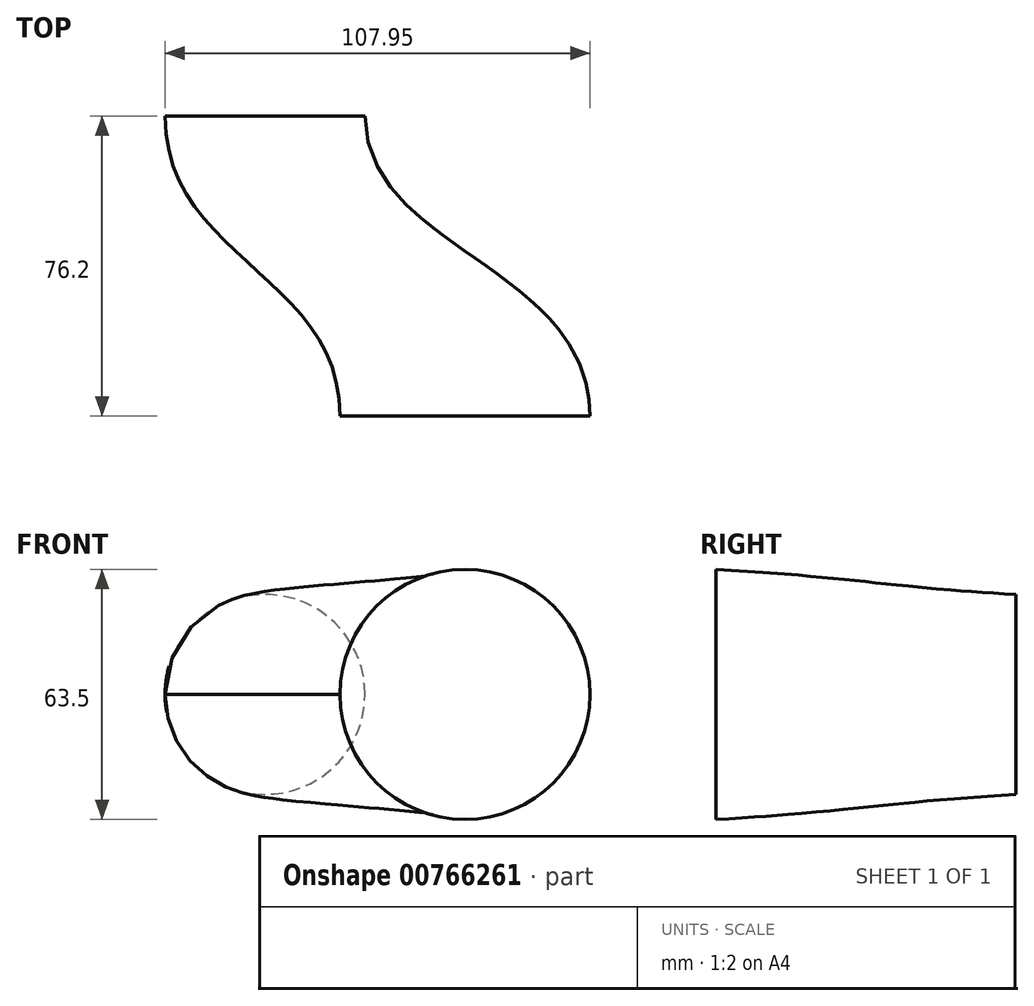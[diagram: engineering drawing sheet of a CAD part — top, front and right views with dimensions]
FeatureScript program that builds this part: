
annotation { "Feature Type Name" : "Feature", "Feature Type Description" : "" }
export const myFeature = defineFeature(function(context is Context, id is Id, definition is map)
    precondition{}
    {
        {
            var Q0;
            Q0=qCreatedBy(makeId("Front.planeOp"),FACE);
            cPlane(context, id + "F0", {"entities" : qUnion([Q0]), "cplaneType" : CPlaneType.OFFSET, "offset" : 76.2 * mm, "width" : 152.4 * mm, "height" : 152.4 * mm});
        }
        {
            var Q0;
            Q0=qCreatedBy(id+"F0.planeOp",FACE);
            var sketch = newSketch(context, id + "F1", { "sketchPlane" : qUnion([Q0])});
            skCircle(sketch, "E0", {"center": v(0, 0) * mm, "radius": 31.75 * mm});
            skSolve(sketch);
        }
        {
            var Q0;
            Q0=qCreatedBy(makeId("Front.planeOp"),FACE);
            var sketch = newSketch(context, id + "F2", { "sketchPlane" : qUnion([Q0])});
            skCircle(sketch, "E1", {"center": v(-50.8, 0) * mm, "radius": 25.4 * mm});
            skLineSegment(sketch, "E2", {"start": v(-50.8, 0) * mm, "end": v(0, 0) * mm, "construction": true});
            skSolve(sketch);
        }
        {
            var Q0;
            Q0=qCreatedBy(makeId("Top.planeOp"),FACE);
            var sketch = newSketch(context, id + "F3", { "sketchPlane" : qUnion([Q0])});
            skFitSpline(sketch, "E3", {"points": [v(-76.2, 0) * mm, v(-31.75, -76.2) * mm], "startDerivative": vector(0, -108.7) * mm, "endDerivative": vector(0, -107.18) * mm});
            skSolve(sketch);
        }
        {
            var Q0;
            Q0=qCreatedBy(makeId("Top.planeOp"),FACE);
            var sketch = newSketch(context, id + "F4", { "sketchPlane" : qUnion([Q0])});
            skFitSpline(sketch, "E4", {"points": [v(-25.4, 0) * mm, v(31.75, -76.2) * mm], "startDerivative": vector(0, -101.66) * mm, "endDerivative": vector(0, -114.17) * mm});
            skSolve(sketch);
        }
        {
            var Q0;
            Q0=makeQuery(id+"F2.imprint","IMPRINT",FACE,{"disambiguationData":[TD([[makeQuery(id+"F2.imprint","IMPRINT",EDGE,{"derivedFrom":sQuery(id+"F2.wireOp",EDGE,"E1")}),1.0]])]});
            var Q1;
            Q1=makeQuery(id+"F1.imprint","IMPRINT",FACE,{"disambiguationData":[TD([[makeQuery(id+"F1.imprint","IMPRINT",EDGE,{"derivedFrom":sQuery(id+"F1.wireOp",EDGE,"E0")}),1.0]])]});
            var Q2;
            Q2 = qConstructionFilter(qBodyType(qCreatedBy(id + "F3" ,EDGE), BodyType.WIRE), ConstructionObject.NO);
            var Q3;
            Q3 = qConstructionFilter(qBodyType(qCreatedBy(id + "F4" ,EDGE), BodyType.WIRE), ConstructionObject.NO);
            var Q4;
            Q4=sQuery(id+"F3.wireOp",VERTEX,"qpPcSAEk-Yxff-x6JP-xup5-S4P08pdUFl33.start");
            var Q5;
            Q5=sQuery(id+"F3.wireOp",VERTEX,"snNEfOa5-MTmY-YXjU-iu0s-ZxJhTdPCbkap.start");
            loft(context, id + "F5", {"addGuides" : true, "sheetProfilesArray" : [{ "sheetProfileEntities" : qUnion([Q0]) }, { "sheetProfileEntities" : qUnion([Q1]) }], "guidesArray" : [{ "guideEntities" : qUnion([Q2]), "guideDerivativeType" : LoftGuideDerivativeType.DEFAULT, "guideDerivativeMagnitude" : 1 }, { "guideEntities" : qUnion([Q3]), "guideDerivativeType" : LoftGuideDerivativeType.DEFAULT, "guideDerivativeMagnitude" : 1 }], "matchConnections" : true, "connections" : [{ "connectionEntities" : qUnion([Q4, Q5]), "connectionEdgeQueries" : qUnion([]), "connectionEdgeParameters" : [] }]});
        }
    });
